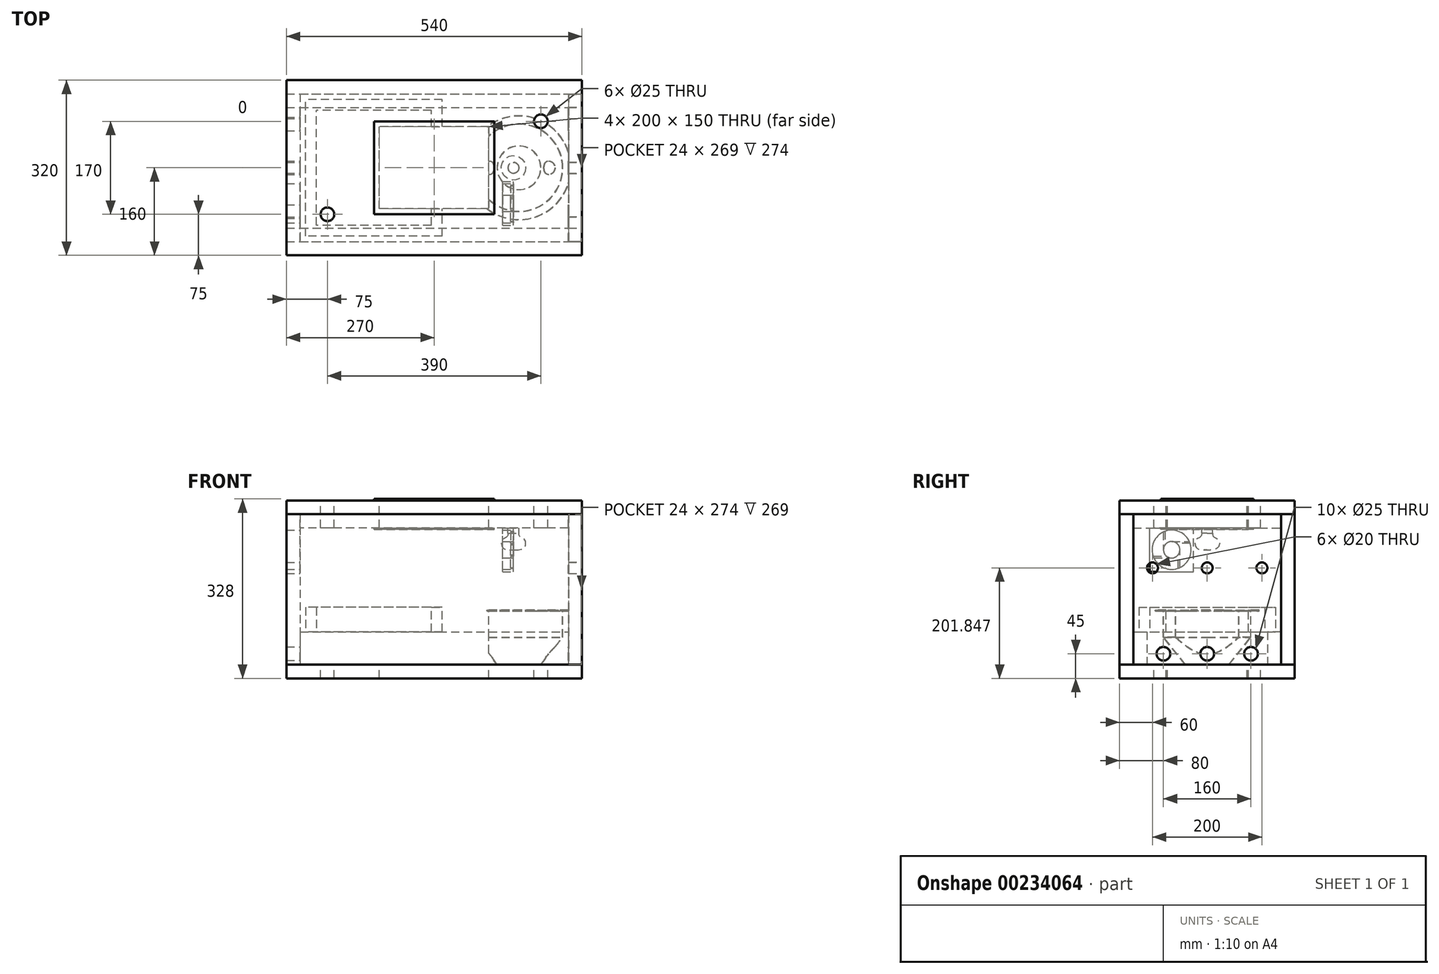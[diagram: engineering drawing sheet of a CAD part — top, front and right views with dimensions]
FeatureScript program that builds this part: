
annotation { "Feature Type Name" : "Feature", "Feature Type Description" : "" }
export const myFeature = defineFeature(function(context is Context, id is Id, definition is map)
    precondition{}
    {
        {
            assignVariable(context, id + "F0", {"name" : "Thickness", "anyValue" : 25});
        }
        {
            var Q0;
            Q0=qCreatedBy(makeId("Top.planeOp"),FACE);
            var sketch = newSketch(context, id + "F1", { "sketchPlane" : qUnion([Q0])});
            skLineSegment(sketch, "E0.bottom", {"start": v(270, -160) * mm, "end": v(-270, -160) * mm});
            skLineSegment(sketch, "E0.top", {"start": v(270, 160) * mm, "end": v(-270, 160) * mm});
            skLineSegment(sketch, "E0.left", {"start": v(270, -160) * mm, "end": v(270, 160) * mm});
            skLineSegment(sketch, "E0.right", {"start": v(-270, -160) * mm, "end": v(-270, 160) * mm});
            skPoint(sketch, "E0.middle", {"position": v(0, 0) * mm});
            skSolve(sketch);
        }
        {
            var Q0;
            Q0=qSketchRegion(id+"F1",true);
            extrude(context, id + "F2", {"entities" : qUnion([Q0]), "depth" : (getVariable(context, 'Thickness')) * mm});
        }
        {
            var Q0;
            Q0=makeQuery(id+"F2.opExtrude","CAP_FACE",FACE,{"disambiguationData":[OSD([sQuery(id+"F1.wireOp",EDGE,"E0.bottom"),sQuery(id+"F1.wireOp",EDGE,"E0.top"),sQuery(id+"F1.wireOp",EDGE,"E0.left"),sQuery(id+"F1.wireOp",EDGE,"E0.right")])],"isStart":false});
            var sketch = newSketch(context, id + "F3", { "sketchPlane" : qUnion([Q0])});
            skLineSegment(sketch, "E1.bottom", {"start": v(-270, -160) * mm, "end": v(270, -160) * mm});
            skLineSegment(sketch, "E1.top", {"start": v(-270, -135) * mm, "end": v(270, -135) * mm});
            skLineSegment(sketch, "E1.left", {"start": v(-270, -160) * mm, "end": v(-270, -135) * mm});
            skLineSegment(sketch, "E1.right", {"start": v(270, -160) * mm, "end": v(270, -135) * mm});
            skLineSegment(sketch, "E2.bottom", {"start": v(-270, 160) * mm, "end": v(270, 160) * mm});
            skLineSegment(sketch, "E2.top", {"start": v(-270, 135) * mm, "end": v(270, 135) * mm});
            skLineSegment(sketch, "E2.left", {"start": v(-270, 160) * mm, "end": v(-270, 135) * mm});
            skLineSegment(sketch, "E2.right", {"start": v(270, 160) * mm, "end": v(270, 135) * mm});
            skSolve(sketch);
        }
        {
            var Q0;
            Q0=qSketchRegion(id+"F3",true);
            extrude(context, id + "F4", {"entities" : qUnion([Q0]), "depth" : (300 - getVariable(context, 'Thickness')) * mm});
        }
        {
            var Q0;
            Q0=makeQuery(id+"F2.opExtrude","CAP_FACE",FACE,{"disambiguationData":[OSD([sQuery(id+"F1.wireOp",EDGE,"E0.bottom"),sQuery(id+"F1.wireOp",EDGE,"E0.top"),sQuery(id+"F1.wireOp",EDGE,"E0.left"),sQuery(id+"F1.wireOp",EDGE,"E0.right")])],"isStart":false});
            var sketch = newSketch(context, id + "F5", { "sketchPlane" : qUnion([Q0])});
            skLineSegment(sketch, "E3.bottom", {"start": v(-270, 135) * mm, "end": v(-245, 135) * mm});
            skLineSegment(sketch, "E3.top", {"start": v(-270, -135) * mm, "end": v(-245, -135) * mm});
            skLineSegment(sketch, "E3.left", {"start": v(-270, 135) * mm, "end": v(-270, -135) * mm});
            skLineSegment(sketch, "E3.right", {"start": v(-245, 135) * mm, "end": v(-245, -135) * mm});
            skLineSegment(sketch, "E4.bottom", {"start": v(245, 135) * mm, "end": v(270, 135) * mm});
            skLineSegment(sketch, "E4.top", {"start": v(245, -135) * mm, "end": v(270, -135) * mm});
            skLineSegment(sketch, "E4.left", {"start": v(245, 135) * mm, "end": v(245, -135) * mm});
            skLineSegment(sketch, "E4.right", {"start": v(270, 135) * mm, "end": v(270, -135) * mm});
            skSolve(sketch);
        }
        {
            var Q0;
            Q0=qSketchRegion(id+"F5",true);
            var Q1;
            Q1=makeQuery(id+"F4.opExtrude","CAP_FACE",FACE,{"disambiguationData":[OSD([sQuery(id+"F3.wireOp",EDGE,"E2.bottom"),sQuery(id+"F3.wireOp",EDGE,"E2.top"),sQuery(id+"F3.wireOp",EDGE,"E2.left"),sQuery(id+"F3.wireOp",EDGE,"E2.right")])],"isStart":false});
            extrude(context, id + "F6", {"entities" : qUnion([Q0]), "endBound" : BoundingType.UP_TO_SURFACE, "endBoundEntityFace" : qUnion([Q1]), "depth" : 25 * mm});
        }
        {
            var Q0;
            Q0=makeQuery(id+"F4.opExtrude","CAP_FACE",FACE,{"disambiguationData":[OSD([sQuery(id+"F3.wireOp",EDGE,"E2.bottom"),sQuery(id+"F3.wireOp",EDGE,"E2.top"),sQuery(id+"F3.wireOp",EDGE,"E2.left"),sQuery(id+"F3.wireOp",EDGE,"E2.right")])],"isStart":false});
            var sketch = newSketch(context, id + "F7", { "sketchPlane" : qUnion([Q0])});
            skLineSegment(sketch, "E5.bottom", {"start": v(245, -135) * mm, "end": v(-245, -135) * mm});
            skLineSegment(sketch, "E5.top", {"start": v(245, 135) * mm, "end": v(-245, 135) * mm});
            skLineSegment(sketch, "E5.left", {"start": v(245, -135) * mm, "end": v(245, 135) * mm});
            skLineSegment(sketch, "E5.right", {"start": v(-245, -135) * mm, "end": v(-245, 135) * mm});
            skPoint(sketch, "E5.middle", {"position": v(0, 0) * mm});
            skSolve(sketch);
        }
        {
            var Q0;
            Q0=qSketchRegion(id+"F7",true);
            extrude(context, id + "F8", {"entities" : qUnion([Q0]), "oppositeDirection" : true, "depth" : (getVariable(context, 'Thickness')) * mm});
        }
        {
            var Q0;
            Q0=makeQuery(id+"F2.opExtrude","CAP_FACE",FACE,{"disambiguationData":[OSD([sQuery(id+"F1.wireOp",EDGE,"E0.bottom"),sQuery(id+"F1.wireOp",EDGE,"E0.top"),sQuery(id+"F1.wireOp",EDGE,"E0.left"),sQuery(id+"F1.wireOp",EDGE,"E0.right")])],"isStart":false});
            var sketch = newSketch(context, id + "F9", { "sketchPlane" : qUnion([Q0])});
            skLineSegment(sketch, "E6.bottom", {"start": v(100, -75) * mm, "end": v(-100, -75) * mm});
            skLineSegment(sketch, "E6.top", {"start": v(100, 75) * mm, "end": v(-100, 75) * mm});
            skLineSegment(sketch, "E6.left", {"start": v(100, -75) * mm, "end": v(100, 75) * mm});
            skLineSegment(sketch, "E6.right", {"start": v(-100, -75) * mm, "end": v(-100, 75) * mm});
            skPoint(sketch, "E6.middle", {"position": v(0, 0) * mm});
            skSolve(sketch);
        }
        {
            var Q0;
            Q0=qSketchRegion(id+"F9",true);
            extrude(context, id + "F10", {"entities" : qUnion([Q0]), "operationType" : NewBodyOperationType.REMOVE, "endBound" : BoundingType.THROUGH_ALL, "oppositeDirection" : true, "depth" : 25 * mm});
        }
        {
            var Q0;
            Q0=makeQuery(id+"F2.opExtrude","CAP_FACE",FACE,{"disambiguationData":[OSD([sQuery(id+"F1.wireOp",EDGE,"E0.bottom"),sQuery(id+"F1.wireOp",EDGE,"E0.top"),sQuery(id+"F1.wireOp",EDGE,"E0.left"),sQuery(id+"F1.wireOp",EDGE,"E0.right")])],"isStart":false});
            var sketch = newSketch(context, id + "F11", { "sketchPlane" : qUnion([Q0])});
            skLineSegment(sketch, "E7.bottom", {"start": v(-245, -135) * mm, "end": v(245, -135) * mm});
            skLineSegment(sketch, "E7.top", {"start": v(-245, -110) * mm, "end": v(245, -110) * mm});
            skLineSegment(sketch, "E7.left", {"start": v(-245, -135) * mm, "end": v(-245, -110) * mm});
            skLineSegment(sketch, "E7.right", {"start": v(245, -135) * mm, "end": v(245, -110) * mm});
            skLineSegment(sketch, "E8.bottom", {"start": v(-245, 135) * mm, "end": v(245, 135) * mm});
            skLineSegment(sketch, "E8.top", {"start": v(-245, 110) * mm, "end": v(245, 110) * mm});
            skLineSegment(sketch, "E8.left", {"start": v(-245, 135) * mm, "end": v(-245, 110) * mm});
            skLineSegment(sketch, "E8.right", {"start": v(245, 135) * mm, "end": v(245, 110) * mm});
            skSolve(sketch);
        }
        {
            var Q0;
            Q0=qSketchRegion(id+"F11",true);
            extrude(context, id + "F12", {"entities" : qUnion([Q0]), "depth" : 60 * mm});
        }
        {
            var Q0;
            Q0=makeQuery(id+"F2.opExtrude","SWEPT_FACE",FACE,{"disambiguationData":[OSD([sQuery(id+"F1.wireOp",EDGE,"E0.left")])]});
            var sketch = newSketch(context, id + "F13", { "sketchPlane" : qUnion([Q0])});
            skCircle(sketch, "E9", {"center": v(0, 201.85) * mm, "radius": 10 * mm});
            skCircle(sketch, "E10.1.0.0", {"center": v(100, 201.85) * mm, "radius": 10 * mm});
            skLineSegment(sketch, "E10.direction1", {"start": v(0, 201.85) * mm, "end": v(100, 201.85) * mm, "construction": true});
            skCircle(sketch, "E11.1.0.0", {"center": v(-100, 201.85) * mm, "radius": 10 * mm});
            skLineSegment(sketch, "E11.direction1", {"start": v(0, 201.85) * mm, "end": v(-100, 201.85) * mm, "construction": true});
            skSolve(sketch);
        }
        {
            var Q0;
            Q0=qSketchRegion(id+"F13",true);
            extrude(context, id + "F14", {"entities" : qUnion([Q0]), "operationType" : NewBodyOperationType.REMOVE, "endBound" : BoundingType.THROUGH_ALL, "oppositeDirection" : true, "depth" : 25 * mm});
        }
        {
            var Q0;
            Q0=makeQuery(id+"F8.opExtrude","CAP_FACE",FACE,{"disambiguationData":[OSD([sQuery(id+"F7.wireOp",EDGE,"E5.bottom"),sQuery(id+"F7.wireOp",EDGE,"E5.top"),sQuery(id+"F7.wireOp",EDGE,"E5.left"),sQuery(id+"F7.wireOp",EDGE,"E5.right")])],"isStart":false});
            var sketch = newSketch(context, id + "F15", { "sketchPlane" : qUnion([Q0])});
            skLineSegment(sketch, "E12.bottom", {"start": v(125, 105) * mm, "end": v(145, 105) * mm});
            skLineSegment(sketch, "E12.top", {"start": v(125, 25) * mm, "end": v(145, 25) * mm});
            skLineSegment(sketch, "E12.left", {"start": v(125, 105) * mm, "end": v(125, 25) * mm});
            skLineSegment(sketch, "E12.right", {"start": v(145, 105) * mm, "end": v(145, 25) * mm});
            skSolve(sketch);
        }
        {
            var Q0;
            Q0=qSketchRegion(id+"F15",true);
            extrude(context, id + "F16", {"entities" : qUnion([Q0]), "depth" : 80 * mm});
        }
        {
            var Q0;
            Q0=makeQuery(id+"F8.opExtrude","CAP_FACE",FACE,{"disambiguationData":[OSD([sQuery(id+"F7.wireOp",EDGE,"E5.bottom"),sQuery(id+"F7.wireOp",EDGE,"E5.top"),sQuery(id+"F7.wireOp",EDGE,"E5.left"),sQuery(id+"F7.wireOp",EDGE,"E5.right")])],"isStart":false});
            var sketch = newSketch(context, id + "F17", { "sketchPlane" : qUnion([Q0])});
            skCircle(sketch, "E13", {"center": v(145, 0) * mm, "radius": 10 * mm});
            skSolve(sketch);
        }
        {
            var Q0;
            Q0=qSketchRegion(id+"F17",true);
            extrude(context, id + "F18", {"entities" : qUnion([Q0]), "depth" : 10 * mm});
        }
        {
            var Q0;
            Q0=qCreatedBy(makeId("Front.planeOp"),FACE);
            var sketch = newSketch(context, id + "F19", { "sketchPlane" : qUnion([Q0])});
            skLineSegment(sketch, "E14", {"start": v(135, 270) * mm, "end": v(135, 280) * mm, "construction": true});
            skLineSegment(sketch, "E15", {"start": v(155, 280) * mm, "end": v(155, 265) * mm, "construction": true});
            skLineSegment(sketch, "E16", {"start": v(145, 286.73) * mm, "end": v(145, 229.32) * mm, "construction": true});
            skFitSpline(sketch, "E17", {"points": [v(145, 235) * mm, v(163.74, 238.24) * mm, v(165.15, 253.78) * mm, v(155, 265) * mm], "startDerivative": vector(37.36, -1.64) * mm, "endDerivative": vector(2.37, 84.3) * mm});
            skLineSegment(sketch, "E18", {"start": v(145, 235) * mm, "end": v(145, 265) * mm});
            skLineSegment(sketch, "E19", {"start": v(145, 265) * mm, "end": v(155, 265) * mm});
            skSolve(sketch);
        }
        {
            var Q0;
            Q0=qSketchRegion(id+"F19",true);
            var Q1;
            Q1=sQuery(id+"F19.wireOp",EDGE,"E16");
            revolve(context, id + "F20", {"operationType" : NewBodyOperationType.ADD, "entities" : qUnion([Q0]), "axis" : qUnion([Q1]), "revolveType" : RevolveType.FULL});
        }
        {
            var Q0;
            Q0=makeQuery(id+"F16.opExtrude","SWEPT_FACE",FACE,{"disambiguationData":[OSD([sQuery(id+"F15.wireOp",EDGE,"E12.right")])]});
            var sketch = newSketch(context, id + "F21", { "sketchPlane" : qUnion([Q0])});
            skCircle(sketch, "E20", {"center": v(-65, 235) * mm, "radius": 35.8 * mm});
            skPoint(sketch, "E20.centerSnap0", {"position": v(-65, 195) * mm});
            skPoint(sketch, "E20.centerSnap1", {"position": v(-105, 235) * mm});
            skSolve(sketch);
        }
        {
            var Q0;
            Q0=qSketchRegion(id+"F21",true);
            extrude(context, id + "F22", {"entities" : qUnion([Q0]), "operationType" : NewBodyOperationType.REMOVE, "endBound" : BoundingType.THROUGH_ALL, "oppositeDirection" : true, "depth" : 25 * mm});
        }
        {
            var Q0;
            Q0=makeQuery(id+"F12.opExtrude","CAP_FACE",FACE,{"disambiguationData":[OSD([sQuery(id+"F11.wireOp",EDGE,"E8.bottom"),sQuery(id+"F11.wireOp",EDGE,"E8.top"),sQuery(id+"F11.wireOp",EDGE,"E8.left"),sQuery(id+"F11.wireOp",EDGE,"E8.right")])],"isStart":false});
            var sketch = newSketch(context, id + "F23", { "sketchPlane" : qUnion([Q0])});
            skLineSegment(sketch, "E21.bottom", {"start": v(15, -125) * mm, "end": v(-235, -125) * mm});
            skLineSegment(sketch, "E21.top", {"start": v(15, 125) * mm, "end": v(-235, 125) * mm});
            skLineSegment(sketch, "E21.left", {"start": v(15, -125) * mm, "end": v(15, 125) * mm});
            skLineSegment(sketch, "E21.right", {"start": v(-235, -125) * mm, "end": v(-235, 125) * mm});
            skLineSegment(sketch, "E22.bottom", {"start": v(-5, -105) * mm, "end": v(-215, -105) * mm});
            skLineSegment(sketch, "E22.top", {"start": v(-5, 105) * mm, "end": v(-215, 105) * mm});
            skLineSegment(sketch, "E22.left", {"start": v(-5, -105) * mm, "end": v(-5, 105) * mm});
            skLineSegment(sketch, "E22.right", {"start": v(-215, -105) * mm, "end": v(-215, 105) * mm});
            skSolve(sketch);
        }
        {
            var Q0;
            Q0=qSketchRegion(id+"F23",true);
            extrude(context, id + "F24", {"entities" : qUnion([Q0]), "depth" : 45 * mm});
        }
        {
            var Q0;
            Q0=makeQuery(id+"F16.opExtrude","SWEPT_FACE",FACE,{"disambiguationData":[OSD([sQuery(id+"F15.wireOp",EDGE,"E12.right")])]});
            var sketch = newSketch(context, id + "F25", { "sketchPlane" : qUnion([Q0])});
            skCircle(sketch, "E23", {"center": v(-65, 235) * mm, "radius": 15 * mm});
            skSolve(sketch);
        }
        {
            var Q0;
            Q0=qSketchRegion(id+"F25",true);
            var Q1;
            Q1=makeQuery(id+"F16.opExtrude","SWEPT_FACE",FACE,{"disambiguationData":[OSD([sQuery(id+"F15.wireOp",EDGE,"E12.left")])]});
            extrude(context, id + "F26", {"entities" : qUnion([Q0]), "endBound" : BoundingType.UP_TO_SURFACE, "oppositeDirection" : true, "endBoundEntityFace" : qUnion([Q1]), "depth" : 25 * mm});
        }
        {
            var Q0;
            Q0=makeQuery(id+"F16.opExtrude","SWEPT_FACE",FACE,{"disambiguationData":[OSD([sQuery(id+"F15.wireOp",EDGE,"E12.right")])]});
            var sketch = newSketch(context, id + "F27", { "sketchPlane" : qUnion([Q0])});
            skLineSegment(sketch, "E24", {"start": v(-65, 250) * mm, "end": v(-32.5, 250) * mm});
            skLineSegment(sketch, "E25", {"start": v(-31.27, 247) * mm, "end": v(-74, 247) * mm});
            skLineSegment(sketch, "E26", {"start": v(-98.73, 223) * mm, "end": v(-56, 223) * mm});
            skLineSegment(sketch, "E27", {"start": v(-97.5, 220) * mm, "end": v(-65, 220) * mm});
            skLineSegment(sketch, "E28", {"start": v(-53, 201.27) * mm, "end": v(-53, 244) * mm});
            skLineSegment(sketch, "E29", {"start": v(-50, 202.5) * mm, "end": v(-50, 235) * mm});
            skLineSegment(sketch, "E30", {"start": v(-80, 267.5) * mm, "end": v(-80, 235) * mm});
            skLineSegment(sketch, "E31", {"start": v(-77, 268.73) * mm, "end": v(-77, 226) * mm});
            skLineSegment(sketch, "E32", {"start": v(-56, 223) * mm, "end": v(-65, 220) * mm});
            skLineSegment(sketch, "E33", {"start": v(-97.5, 220) * mm, "end": v(-98.73, 223) * mm});
            skLineSegment(sketch, "E34", {"start": v(-80, 267.5) * mm, "end": v(-77, 268.73) * mm});
            skLineSegment(sketch, "E35", {"start": v(-80, 235) * mm, "end": v(-77, 226) * mm});
            skLineSegment(sketch, "E36", {"start": v(-65, 250) * mm, "end": v(-74, 247) * mm});
            skLineSegment(sketch, "E37", {"start": v(-50, 235) * mm, "end": v(-53, 244) * mm});
            skLineSegment(sketch, "E38", {"start": v(-53, 201.27) * mm, "end": v(-50, 202.5) * mm});
            skLineSegment(sketch, "E39", {"start": v(-31.27, 247) * mm, "end": v(-32.5, 250) * mm});
            skLineSegment(sketch, "E40", {"start": v(-77, 268.73) * mm, "end": v(-80, 267.5) * mm});
            skSolve(sketch);
        }
        {
            var Q0;
            Q0=qSketchRegion(id+"F27",true);
            extrude(context, id + "F28", {"entities" : qUnion([Q0]), "operationType" : NewBodyOperationType.ADD, "oppositeDirection" : true, "depth" : 5 * mm});
        }
        {
            var Q0;
            Q0=makeQuery(id+"F8.opExtrude","CAP_FACE",FACE,{"disambiguationData":[OSD([sQuery(id+"F7.wireOp",EDGE,"E5.bottom"),sQuery(id+"F7.wireOp",EDGE,"E5.top"),sQuery(id+"F7.wireOp",EDGE,"E5.left"),sQuery(id+"F7.wireOp",EDGE,"E5.right")])],"isStart":true});
            var sketch = newSketch(context, id + "F29", { "sketchPlane" : qUnion([Q0])});
            skLineSegment(sketch, "E41.bottom", {"start": v(-270, 160) * mm, "end": v(270, 160) * mm});
            skLineSegment(sketch, "E41.top", {"start": v(-270, -160) * mm, "end": v(270, -160) * mm});
            skLineSegment(sketch, "E41.left", {"start": v(-270, 160) * mm, "end": v(-270, -160) * mm});
            skLineSegment(sketch, "E41.right", {"start": v(270, 160) * mm, "end": v(270, -160) * mm});
            skSolve(sketch);
        }
        {
            var Q0;
            Q0=qSketchRegion(id+"F29",true);
            extrude(context, id + "F30", {"entities" : qUnion([Q0]), "depth" : (getVariable(context, 'Thickness')) * mm});
        }
        {
            var Q0;
            Q0=makeQuery(id+"F30.opExtrude","CAP_FACE",FACE,{"disambiguationData":[OSD([sQuery(id+"F29.wireOp",EDGE,"E41.bottom"),sQuery(id+"F29.wireOp",EDGE,"E41.top"),sQuery(id+"F29.wireOp",EDGE,"E41.left"),sQuery(id+"F29.wireOp",EDGE,"E41.right")])],"isStart":false});
            var sketch = newSketch(context, id + "F31", { "sketchPlane" : qUnion([Q0])});
            skLineSegment(sketch, "E42.bottom", {"start": v(-110, 85) * mm, "end": v(110, 85) * mm});
            skLineSegment(sketch, "E42.top", {"start": v(-110, -85) * mm, "end": v(110, -85) * mm});
            skLineSegment(sketch, "E42.left", {"start": v(-110, 85) * mm, "end": v(-110, -85) * mm});
            skLineSegment(sketch, "E42.right", {"start": v(110, 85) * mm, "end": v(110, -85) * mm});
            skSolve(sketch);
        }
        {
            var Q0;
            Q0=qSketchRegion(id+"F31",true);
            extrude(context, id + "F32", {"entities" : qUnion([Q0]), "depth" : 3 * mm});
        }
        {
            var Q0;
            Q0=makeQuery(id+"FPmrWlQUmZ3GT1M_39.opPattern","COPY",BODY,{"derivedFrom":makeQuery(id+"F32.opExtrude","SWEPT_BODY",BODY,{"disambiguationData":[OSD([sQuery(id+"F31.wireOp",EDGE,"E42.bottom"),sQuery(id+"F31.wireOp",EDGE,"E42.top"),sQuery(id+"F31.wireOp",EDGE,"E42.left"),sQuery(id+"F31.wireOp",EDGE,"E42.right")])]}),"instanceName":"1"});
            var Q1;
            Q1=makeQuery(id+"F32.opExtrude","SWEPT_BODY",BODY,{"disambiguationData":[OSD([sQuery(id+"F31.wireOp",EDGE,"E42.bottom"),sQuery(id+"F31.wireOp",EDGE,"E42.top"),sQuery(id+"F31.wireOp",EDGE,"E42.left"),sQuery(id+"F31.wireOp",EDGE,"E42.right")])]});
            var Q2;
            Q2=makeQuery(id+"F8.opExtrude","SWEPT_BODY",BODY,{"disambiguationData":[OSD([sQuery(id+"F7.wireOp",EDGE,"E5.bottom"),sQuery(id+"F7.wireOp",EDGE,"E5.top"),sQuery(id+"F7.wireOp",EDGE,"E5.left"),sQuery(id+"F7.wireOp",EDGE,"E5.right")])]});
            booleanBodies(context, id + "F33", {"operationType" : BooleanOperationType.SUBTRACTION, "tools" : qUnion([Q0, Q1]), "targets" : qUnion([Q2]), "keepTools" : true});
        }
        {
            var Q0;
            Q0=makeQuery(id+"F2.opExtrude","CAP_FACE",FACE,{"disambiguationData":[OSD([sQuery(id+"F1.wireOp",EDGE,"E0.bottom"),sQuery(id+"F1.wireOp",EDGE,"E0.top"),sQuery(id+"F1.wireOp",EDGE,"E0.left"),sQuery(id+"F1.wireOp",EDGE,"E0.right")])],"isStart":false});
            var sketch = newSketch(context, id + "F34", { "sketchPlane" : qUnion([Q0])});
            skCircle(sketch, "E43", {"center": v(155, 0) * mm, "radius": 40 * mm});
            skLineSegment(sketch, "E44", {"start": v(155, 0) * mm, "end": v(88.88, 0) * mm, "construction": true});
            skLineSegment(sketch, "E45", {"start": v(155, 0) * mm, "end": v(155, 60.62) * mm, "construction": true});
            skSolve(sketch);
        }
        {
            var Q0;
            Q0=makeQuery(id+"F34.imprint","IMPRINT",FACE,{"disambiguationData":[TD([[makeQuery(id+"F34.imprint","IMPRINT",EDGE,{"derivedFrom":sQuery(id+"F34.wireOp",EDGE,"E43")}),-1.0]])]});
            cPlane(context, id + "F35", {"entities" : qUnion([Q0]), "cplaneType" : CPlaneType.OFFSET, "offset" : 50 * mm, "width" : 150 * mm, "height" : 150 * mm});
        }
        {
            var Q0;
            Q0=qCreatedBy(id+"F35.planeOp",FACE);
            var sketch = newSketch(context, id + "F36", { "sketchPlane" : qUnion([Q0])});
            skCircle(sketch, "E46", {"center": v(155, 0) * mm, "radius": 80 * mm});
            skSolve(sketch);
        }
        {
            var Q0;
            Q0=qCreatedBy(id+"F35.planeOp",FACE);
            cPlane(context, id + "F37", {"entities" : qUnion([Q0]), "cplaneType" : CPlaneType.OFFSET, "offset" : 50 * mm, "width" : 150 * mm, "height" : 150 * mm});
        }
        {
            var Q1;
            Q1=makeQuery(id+"F34.imprint","IMPRINT",FACE,{"disambiguationData":[TD([[makeQuery(id+"F34.imprint","IMPRINT",EDGE,{"derivedFrom":sQuery(id+"F34.wireOp",EDGE,"E43")}),1.0]])]});
            var Q2;
            Q2=makeQuery(id+"F36.imprint","IMPRINT",FACE,{"disambiguationData":[TD([[makeQuery(id+"F36.imprint","IMPRINT",EDGE,{"derivedFrom":sQuery(id+"F36.wireOp",EDGE,"E46")}),1.0]])]});
            loft(context, id + "F38", {"sheetProfilesArray" : [{ "sheetProfileEntities" : qUnion([Q1]) }, { "sheetProfileEntities" : qUnion([Q2]) }]});
        }
        {
            var Q0;
            Q0=qCreatedBy(id+"F37.planeOp",FACE);
            var sketch = newSketch(context, id + "F39", { "sketchPlane" : qUnion([Q0])});
            skCircle(sketch, "E47.0", {"center": v(155, 0) * mm, "radius": 80 * mm});
            skSolve(sketch);
        }
        {
            var Q0;
            Q0=qSketchRegion(id+"F39",true);
            var Q1;
            Q1=makeQuery(id+"F38.opLoft","CAP_FACE",FACE,{"disambiguationData":[OSD([makeQuery(id+"F36.imprint","IMPRINT",FACE,{"disambiguationData":[TD([[makeQuery(id+"F36.imprint","IMPRINT",EDGE,{"derivedFrom":sQuery(id+"F36.wireOp",EDGE,"E46")}),1.0]])]})])],"isStart":true});
            extrude(context, id + "F40", {"entities" : qUnion([Q0]), "operationType" : NewBodyOperationType.ADD, "endBound" : BoundingType.UP_TO_SURFACE, "oppositeDirection" : true, "endBoundEntityFace" : qUnion([Q1]), "depth" : 25 * mm});
        }
        {
            var Q0;
            Q0=makeQuery(id+"F40.opExtrude","CAP_FACE",FACE,{"disambiguationData":[OSD([sQuery(id+"F39.wireOp",EDGE,"E47.0")])],"isStart":true});
            var sketch = newSketch(context, id + "F41", { "sketchPlane" : qUnion([Q0])});
            skCircle(sketch, "E48", {"center": v(155, 0) * mm, "radius": 95 * mm});
            skSolve(sketch);
        }
        {
            var Q0;
            Q0=qSketchRegion(id+"F41",true);
            extrude(context, id + "F42", {"entities" : qUnion([Q0]), "operationType" : NewBodyOperationType.ADD, "oppositeDirection" : true, "depth" : 2 * mm});
        }
        {
            var Q0;
            Q0=makeQuery(id+"F42.boolean.opBoolean","MERGE",FACE,{"derivedFrom":[makeQuery(id+"F40.opExtrude","CAP_FACE",FACE,{"disambiguationData":[OSD([sQuery(id+"F39.wireOp",EDGE,"E47.0")])],"isStart":true}),makeQuery(id+"F42.opExtrude","CAP_FACE",FACE,{"disambiguationData":[OSD([sQuery(id+"F41.wireOp",EDGE,"E48")])],"isStart":true})]});
            shell(context, id + "F43", {"entities" : qUnion([Q0]), "thickness" : 0.5 * mm});
        }
        {
            var Q0;
            Q0=makeQuery(id+"F32.opExtrude","SWEPT_BODY",BODY,{"disambiguationData":[OSD([sQuery(id+"F31.wireOp",EDGE,"E42.bottom"),sQuery(id+"F31.wireOp",EDGE,"E42.top"),sQuery(id+"F31.wireOp",EDGE,"E42.left"),sQuery(id+"F31.wireOp",EDGE,"E42.right")])]});
            var Q1;
            Q1=makeQuery(id+"F30.opExtrude","CAP_FACE",FACE,{"disambiguationData":[OSD([sQuery(id+"F29.wireOp",EDGE,"E41.bottom"),sQuery(id+"F29.wireOp",EDGE,"E41.top"),sQuery(id+"F29.wireOp",EDGE,"E41.left"),sQuery(id+"F29.wireOp",EDGE,"E41.right")])],"isStart":true});
            mirror(context, id + "F44", {"entities" : qUnion([Q0]), "mirrorPlane" : qUnion([Q1])});
        }
        {
            var Q0;
            Q0=makeQuery(id+"F30.opExtrude","CAP_FACE",FACE,{"disambiguationData":[OSD([sQuery(id+"F29.wireOp",EDGE,"E41.bottom"),sQuery(id+"F29.wireOp",EDGE,"E41.top"),sQuery(id+"F29.wireOp",EDGE,"E41.left"),sQuery(id+"F29.wireOp",EDGE,"E41.right")])],"isStart":false});
            var sketch = newSketch(context, id + "F45", { "sketchPlane" : qUnion([Q0])});
            skLineSegment(sketch, "E49.bottom", {"start": v(-100, 75) * mm, "end": v(100, 75) * mm});
            skLineSegment(sketch, "E49.top", {"start": v(-100, -75) * mm, "end": v(100, -75) * mm});
            skLineSegment(sketch, "E49.left", {"start": v(-100, 75) * mm, "end": v(-100, -75) * mm});
            skLineSegment(sketch, "E49.right", {"start": v(100, 75) * mm, "end": v(100, -75) * mm});
            skSolve(sketch);
        }
        {
            var Q0;
            Q0=qSketchRegion(id+"F45",true);
            extrude(context, id + "F46", {"entities" : qUnion([Q0]), "operationType" : NewBodyOperationType.REMOVE, "endBound" : BoundingType.THROUGH_ALL, "oppositeDirection" : true, "depth" : 25 * mm});
        }
        {
            var Q0;
            Q0=makeQuery(id+"F6.opExtrude","SWEPT_FACE",FACE,{"disambiguationData":[OSD([sQuery(id+"F5.wireOp",EDGE,"E4.right")])]});
            var sketch = newSketch(context, id + "F47", { "sketchPlane" : qUnion([Q0])});
            skCircle(sketch, "E50", {"center": v(0, 45) * mm, "radius": 12.5 * mm});
            skCircle(sketch, "E51", {"center": v(-80, 45) * mm, "radius": 12.5 * mm});
            skCircle(sketch, "E52", {"center": v(80, 45) * mm, "radius": 12.5 * mm});
            skSolve(sketch);
        }
        {
            var Q0;
            Q0=qSketchRegion(id+"F47",true);
            extrude(context, id + "F48", {"entities" : qUnion([Q0]), "operationType" : NewBodyOperationType.REMOVE, "endBound" : BoundingType.THROUGH_ALL, "oppositeDirection" : true, "depth" : 25 * mm});
        }
        {
            var Q0;
            Q0=makeQuery(id+"F30.opExtrude","CAP_FACE",FACE,{"disambiguationData":[OSD([sQuery(id+"F29.wireOp",EDGE,"E41.bottom"),sQuery(id+"F29.wireOp",EDGE,"E41.top"),sQuery(id+"F29.wireOp",EDGE,"E41.left"),sQuery(id+"F29.wireOp",EDGE,"E41.right")])],"isStart":false});
            var sketch = newSketch(context, id + "F49", { "sketchPlane" : qUnion([Q0])});
            skCircle(sketch, "E53", {"center": v(-195, -85) * mm, "radius": 12.5 * mm});
            skCircle(sketch, "E54", {"center": v(195, 85) * mm, "radius": 12.5 * mm});
            skSolve(sketch);
        }
        {
            var Q0;
            Q0=qSketchRegion(id+"F49",true);
            extrude(context, id + "F50", {"entities" : qUnion([Q0]), "operationType" : NewBodyOperationType.REMOVE, "endBound" : BoundingType.THROUGH_ALL, "oppositeDirection" : true, "depth" : 25 * mm});
        }
    });
